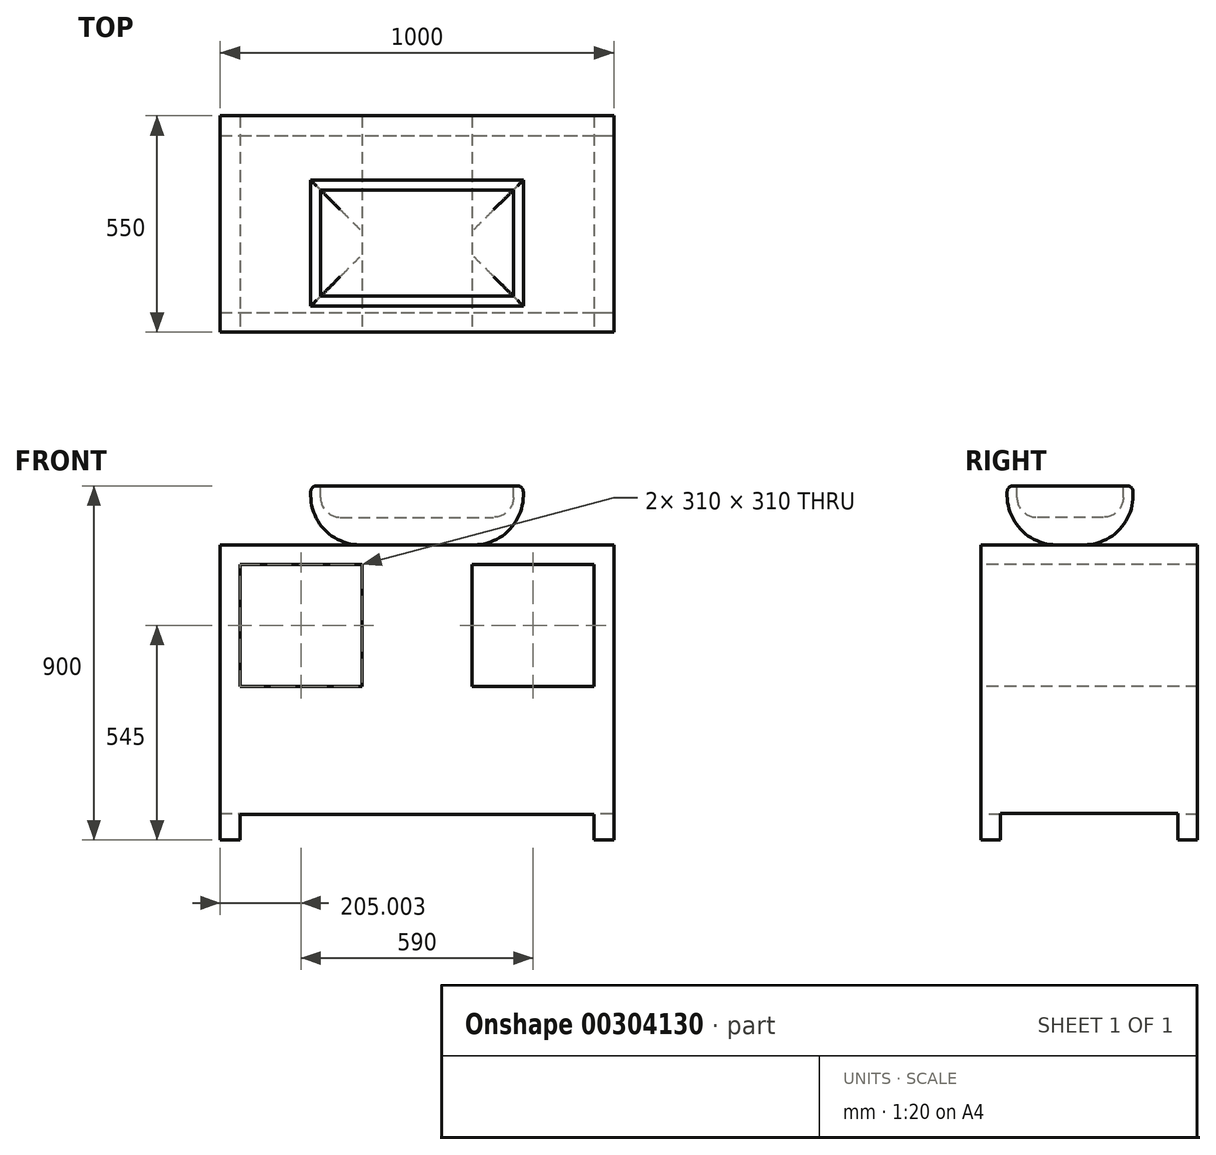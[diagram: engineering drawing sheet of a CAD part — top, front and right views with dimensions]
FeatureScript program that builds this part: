
annotation { "Feature Type Name" : "Feature", "Feature Type Description" : "" }
export const myFeature = defineFeature(function(context is Context, id is Id, definition is map)
    precondition{}
    {
        {
            var Q0;
            Q0=qCreatedBy(makeId("Top.planeOp"),FACE);
            var sketch = newSketch(context, id + "F0", { "sketchPlane" : qUnion([Q0])});
            skLineSegment(sketch, "E0.bottom", {"start": v(-505.84, 288.3) * mm, "end": v(494.16, 288.3) * mm});
            skLineSegment(sketch, "E0.top", {"start": v(-505.84, -261.7) * mm, "end": v(494.16, -261.7) * mm});
            skLineSegment(sketch, "E0.left", {"start": v(-505.84, 288.3) * mm, "end": v(-505.84, -261.7) * mm});
            skLineSegment(sketch, "E0.right", {"start": v(494.16, 288.3) * mm, "end": v(494.16, -261.7) * mm});
            skSolve(sketch);
        }
        {
            var Q0;
            Q0=makeQuery(id+"F0.imprint","IMPRINT",FACE,{"disambiguationData":[TD([[makeQuery(id+"F0.imprint","IMPRINT",EDGE,{"derivedFrom":sQuery(id+"F0.wireOp",EDGE,"E0.bottom")}),-1.0]])]});
            extrude(context, id + "F1", {"entities" : qUnion([Q0]), "depth" : 750 * mm, "offsetDistance" : 25 * mm});
        }
        {
            var Q0;
            Q0=makeQuery(id+"F1.opExtrude","CAP_FACE",FACE,{"disambiguationData":[OSD([sQuery(id+"F0.wireOp",EDGE,"E0.bottom"),sQuery(id+"F0.wireOp",EDGE,"E0.top"),sQuery(id+"F0.wireOp",EDGE,"E0.left"),sQuery(id+"F0.wireOp",EDGE,"E0.right")])],"isStart":false});
            cPlane(context, id + "F2", {"entities" : qUnion([Q0]), "cplaneType" : CPlaneType.OFFSET, "offset" : 0 * mm, "width" : 150 * mm, "height" : 150 * mm});
        }
        {
            var Q0;
            Q0=qCreatedBy(id+"F2.planeOp",FACE);
            var sketch = newSketch(context, id + "F3", { "sketchPlane" : qUnion([Q0])});
            skLineSegment(sketch, "E1.bottom", {"start": v(-275.84, 124.85) * mm, "end": v(264.16, 124.85) * mm});
            skLineSegment(sketch, "E1.top", {"start": v(-275.84, -195.27) * mm, "end": v(264.16, -195.27) * mm});
            skLineSegment(sketch, "E1.left", {"start": v(-275.84, 124.85) * mm, "end": v(-275.84, -195.27) * mm});
            skLineSegment(sketch, "E1.right", {"start": v(264.16, 124.85) * mm, "end": v(264.16, -195.27) * mm});
            skSolve(sketch);
        }
        {
            var Q0;
            Q0=makeQuery(id+"F3.imprint","IMPRINT",FACE,{"disambiguationData":[TD([[makeQuery(id+"F3.imprint","IMPRINT",EDGE,{"derivedFrom":sQuery(id+"F3.wireOp",EDGE,"E1.bottom")}),-1.0]])]});
            extrude(context, id + "F4", {"entities" : qUnion([Q0]), "depth" : 150 * mm, "offsetDistance" : 25 * mm});
        }
        {
            var Q0;
            Q0=makeQuery(id+"F4.opExtrude","CAP_EDGE",EDGE,{"disambiguationData":[OSD([sQuery(id+"F3.wireOp",EDGE,"E1.top")])],"isStart":true});
            var Q1;
            Q1=makeQuery(id+"F4.opExtrude","CAP_EDGE",EDGE,{"disambiguationData":[OSD([sQuery(id+"F3.wireOp",EDGE,"E1.right")])],"isStart":true});
            var Q2;
            Q2=makeQuery(id+"F4.opExtrude","CAP_EDGE",EDGE,{"disambiguationData":[OSD([sQuery(id+"F3.wireOp",EDGE,"E1.bottom")])],"isStart":true});
            var Q3;
            Q3=makeQuery(id+"F4.opExtrude","CAP_EDGE",EDGE,{"disambiguationData":[OSD([sQuery(id+"F3.wireOp",EDGE,"E1.left")])],"isStart":true});
            fillet(context, id + "F5", {"entities" : qUnion([Q0, Q1, Q2, Q3]), "radius" : 125 * mm, "tangentPropagation" : true, "allowEdgeOverflow" : false});
        }
        {
            var Q0;
            Q0=makeQuery(id+"F4.opExtrude","CAP_EDGE",EDGE,{"disambiguationData":[OSD([sQuery(id+"F3.wireOp",EDGE,"E1.top")])],"isStart":false});
            var Q1;
            Q1=makeQuery(id+"F4.opExtrude","CAP_EDGE",EDGE,{"disambiguationData":[OSD([sQuery(id+"F3.wireOp",EDGE,"E1.left")])],"isStart":false});
            var Q2;
            Q2=makeQuery(id+"F4.opExtrude","CAP_EDGE",EDGE,{"disambiguationData":[OSD([sQuery(id+"F3.wireOp",EDGE,"E1.bottom")])],"isStart":false});
            var Q3;
            Q3=makeQuery(id+"F4.opExtrude","CAP_EDGE",EDGE,{"disambiguationData":[OSD([sQuery(id+"F3.wireOp",EDGE,"E1.right")])],"isStart":false});
            fillet(context, id + "F6", {"entities" : qUnion([Q0, Q1, Q2, Q3]), "radius" : 15 * mm, "tangentPropagation" : true, "allowEdgeOverflow" : false});
        }
        {
            var Q0;
            Q0=makeQuery(id+"F4.opExtrude","CAP_FACE",FACE,{"disambiguationData":[OSD([sQuery(id+"F3.wireOp",EDGE,"E1.bottom"),sQuery(id+"F3.wireOp",EDGE,"E1.top"),sQuery(id+"F3.wireOp",EDGE,"E1.left"),sQuery(id+"F3.wireOp",EDGE,"E1.right")])],"isStart":false});
            var sketch = newSketch(context, id + "F7", { "sketchPlane" : qUnion([Q0])});
            skLineSegment(sketch, "E2.bottom", {"start": v(-250.84, 99.85) * mm, "end": v(239.16, 99.85) * mm});
            skLineSegment(sketch, "E2.top", {"start": v(-250.84, -170.27) * mm, "end": v(239.16, -170.27) * mm});
            skLineSegment(sketch, "E2.left", {"start": v(-250.84, 99.85) * mm, "end": v(-250.84, -170.27) * mm});
            skLineSegment(sketch, "E2.right", {"start": v(239.16, 99.85) * mm, "end": v(239.16, -170.27) * mm});
            skSolve(sketch);
        }
        {
            var Q0;
            Q0=makeQuery(id+"F7.imprint","IMPRINT",FACE,{"disambiguationData":[TD([[makeQuery(id+"F7.imprint","IMPRINT",EDGE,{"derivedFrom":sQuery(id+"F7.wireOp",EDGE,"E2.bottom")}),-1.0]])]});
            extrude(context, id + "F8", {"entities" : qUnion([Q0]), "operationType" : NewBodyOperationType.REMOVE, "oppositeDirection" : true, "depth" : 80 * mm, "offsetDistance" : 25 * mm});
        }
        {
            var Q0;
            Q0=makeQuery(id+"F8.boolean.opBoolean","COPY",EDGE,{"derivedFrom":makeQuery(id+"F8.opExtrude","CAP_EDGE",EDGE,{"disambiguationData":[OSD([sQuery(id+"F7.wireOp",EDGE,"E2.bottom")])],"isStart":false})});
            var Q1;
            Q1=makeQuery(id+"F8.boolean.opBoolean","COPY",EDGE,{"derivedFrom":makeQuery(id+"F8.opExtrude","CAP_EDGE",EDGE,{"disambiguationData":[OSD([sQuery(id+"F7.wireOp",EDGE,"E2.left")])],"isStart":false})});
            var Q2;
            Q2=makeQuery(id+"F8.boolean.opBoolean","COPY",EDGE,{"derivedFrom":makeQuery(id+"F8.opExtrude","CAP_EDGE",EDGE,{"disambiguationData":[OSD([sQuery(id+"F7.wireOp",EDGE,"E2.right")])],"isStart":false})});
            var Q3;
            Q3=makeQuery(id+"F8.boolean.opBoolean","COPY",EDGE,{"derivedFrom":makeQuery(id+"F8.opExtrude","CAP_EDGE",EDGE,{"disambiguationData":[OSD([sQuery(id+"F7.wireOp",EDGE,"E2.top")])],"isStart":false})});
            fillet(context, id + "F9", {"entities" : qUnion([Q0, Q1, Q2, Q3]), "radius" : 50 * mm, "tangentPropagation" : true, "allowEdgeOverflow" : false});
        }
        {
            var Q0;
            Q0=makeQuery(id+"F1.opExtrude","SWEPT_FACE",FACE,{"disambiguationData":[OSD([sQuery(id+"F0.wireOp",EDGE,"E0.top")])]});
            var sketch = newSketch(context, id + "F10", { "sketchPlane" : qUnion([Q0])});
            skLineSegment(sketch, "E3.bottom", {"start": v(-455.84, 700) * mm, "end": v(-145.84, 700) * mm});
            skLineSegment(sketch, "E3.top", {"start": v(-455.84, 390) * mm, "end": v(-145.84, 390) * mm});
            skLineSegment(sketch, "E3.left", {"start": v(-455.84, 700) * mm, "end": v(-455.84, 390) * mm});
            skLineSegment(sketch, "E3.right", {"start": v(-145.84, 700) * mm, "end": v(-145.84, 390) * mm});
            skLineSegment(sketch, "E4.bottom", {"start": v(134.16, 700) * mm, "end": v(444.16, 700) * mm});
            skLineSegment(sketch, "E4.top", {"start": v(134.16, 390) * mm, "end": v(444.16, 390) * mm});
            skLineSegment(sketch, "E4.left", {"start": v(134.16, 700) * mm, "end": v(134.16, 390) * mm});
            skLineSegment(sketch, "E4.right", {"start": v(444.16, 700) * mm, "end": v(444.16, 390) * mm});
            skLineSegment(sketch, "E5.bottom", {"start": v(-455.84, 0) * mm, "end": v(444.16, 0) * mm});
            skLineSegment(sketch, "E5.top", {"start": v(-455.84, 64.64) * mm, "end": v(444.16, 64.64) * mm});
            skLineSegment(sketch, "E5.left", {"start": v(-455.84, 0) * mm, "end": v(-455.84, 64.64) * mm});
            skLineSegment(sketch, "E5.right", {"start": v(444.16, 0) * mm, "end": v(444.16, 64.64) * mm});
            skSolve(sketch);
        }
        {
            var Q0;
            Q0=makeQuery(id+"F10.imprint","IMPRINT",FACE,{"disambiguationData":[TD([[makeQuery(id+"F10.imprint","IMPRINT",EDGE,{"derivedFrom":sQuery(id+"F10.wireOp",EDGE,"E3.bottom")}),-1.0]])]});
            var Q1;
            Q1=makeQuery(id+"F10.imprint","IMPRINT",FACE,{"disambiguationData":[TD([[makeQuery(id+"F10.imprint","IMPRINT",EDGE,{"derivedFrom":sQuery(id+"F10.wireOp",EDGE,"E4.bottom")}),-1.0]])]});
            var Q2;
            Q2=makeQuery(id+"F10.imprint","IMPRINT",FACE,{"disambiguationData":[TD([[makeQuery(id+"F10.imprint","IMPRINT",EDGE,{"derivedFrom":sQuery(id+"F10.wireOp",EDGE,"E5.bottom")}),1.0]])]});
            extrude(context, id + "F11", {"entities" : qUnion([Q0, Q1, Q2]), "operationType" : NewBodyOperationType.REMOVE, "endBound" : BoundingType.UP_TO_NEXT, "oppositeDirection" : true, "depth" : 25 * mm, "offsetDistance" : 25 * mm});
        }
        {
            var Q0;
            Q0=makeQuery(id+"F1.opExtrude","SWEPT_FACE",FACE,{"disambiguationData":[OSD([sQuery(id+"F0.wireOp",EDGE,"E0.right")])]});
            var sketch = newSketch(context, id + "F12", { "sketchPlane" : qUnion([Q0])});
            skLineSegment(sketch, "E6.bottom", {"start": v(-211.7, 0) * mm, "end": v(238.3, 0) * mm});
            skLineSegment(sketch, "E6.top", {"start": v(-211.7, 67.74) * mm, "end": v(238.3, 67.74) * mm});
            skLineSegment(sketch, "E6.left", {"start": v(-211.7, 0) * mm, "end": v(-211.7, 67.74) * mm});
            skLineSegment(sketch, "E6.right", {"start": v(238.3, 0) * mm, "end": v(238.3, 67.74) * mm});
            skSolve(sketch);
        }
        {
            var Q0;
            Q0=makeQuery(id+"F12.imprint","IMPRINT",FACE,{"disambiguationData":[TD([[makeQuery(id+"F12.imprint","IMPRINT",EDGE,{"derivedFrom":sQuery(id+"F12.wireOp",EDGE,"E6.bottom")}),-1.0]])]});
            extrude(context, id + "F13", {"entities" : qUnion([Q0]), "operationType" : NewBodyOperationType.REMOVE, "endBound" : BoundingType.THROUGH_ALL, "oppositeDirection" : true, "depth" : 25 * mm, "offsetDistance" : 25 * mm});
        }
    });
